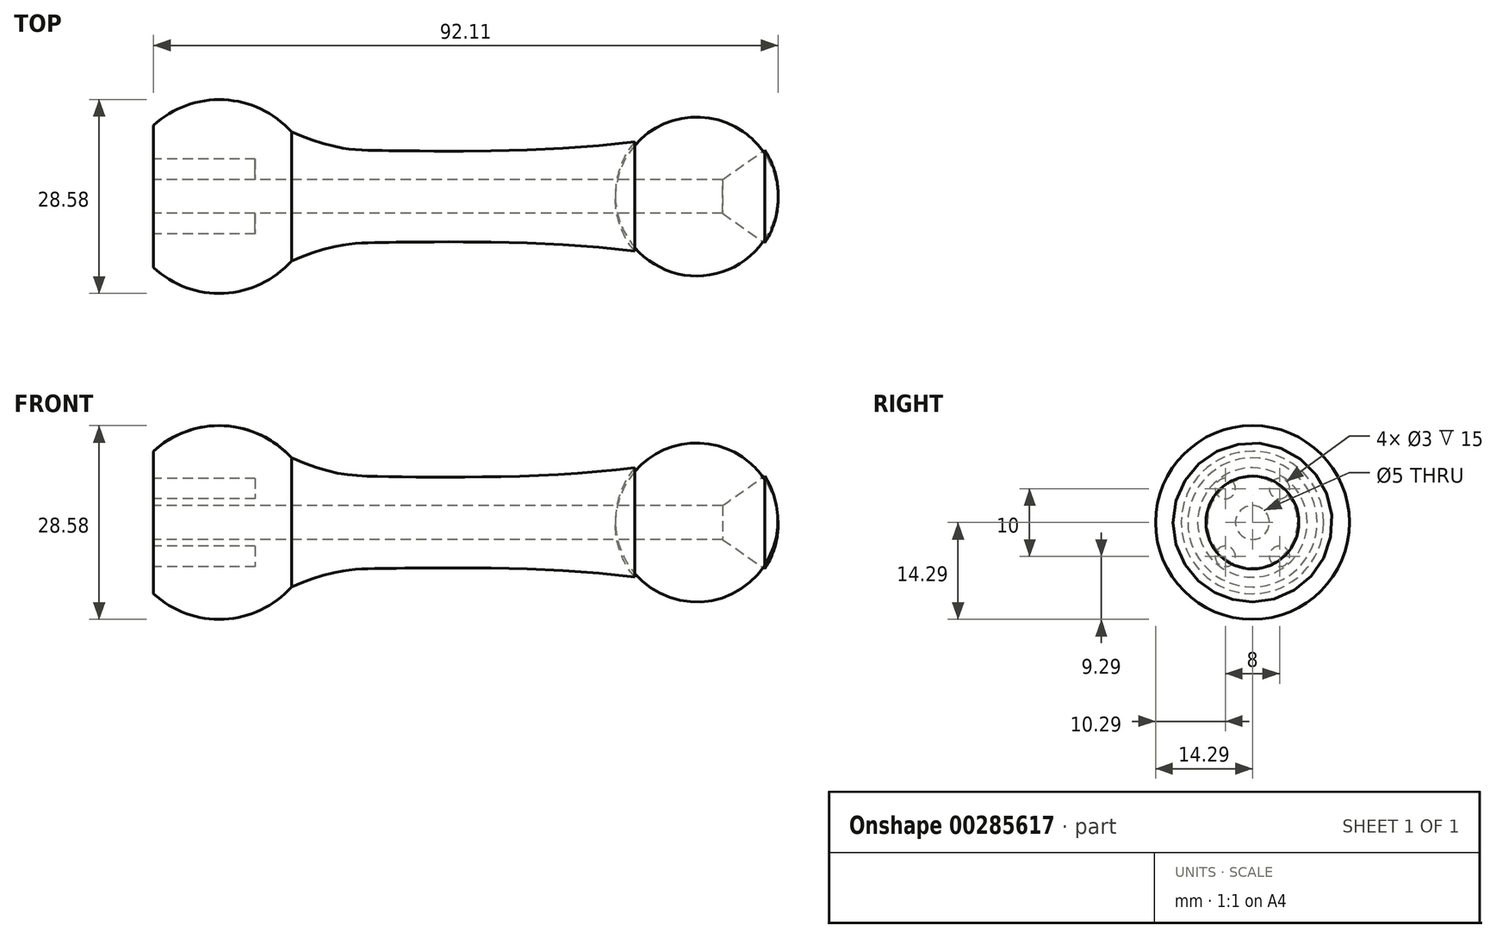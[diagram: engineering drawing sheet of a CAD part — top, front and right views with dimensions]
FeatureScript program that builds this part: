
annotation { "Feature Type Name" : "Feature", "Feature Type Description" : "" }
export const myFeature = defineFeature(function(context is Context, id is Id, definition is map)
    precondition{}
    {
        {
            var Q0;
            Q0=qCreatedBy(makeId("Front.planeOp"),FACE);
            var sketch = newSketch(context, id + "F0", { "sketchPlane" : qUnion([Q0])});
            skLineSegment(sketch, "E0", {"start": v(12.5, 0) * mm, "end": v(57.5, 0) * mm});
            skFitSpline(sketch, "E1", {"points": [v(10.65, 9.52) * mm, v(24.8, 6.77) * mm, v(61.3, 8.08) * mm], "startDerivative": vector(49.03, -20.8) * mm, "endDerivative": vector(62.99, 8.12) * mm});
            skLineSegment(sketch, "E2", {"start": v(12.25, 2.5) * mm, "end": v(74.25, 2.5) * mm});
            skLineSegment(sketch, "E3", {"start": v(74.25, 2.5) * mm, "end": v(80.46, 6.85) * mm});
            skArc(sketch, "E4.trimOffspring", {"start": v(80.46, 6.85) * mm, "mid": v(71.19, 12.25) * mm, "end": v(61.3, 8.08) * mm});
            skPoint(sketch, "E5.end.orphan", {"position": v(82.25, 2.5) * mm});
            skPoint(sketch, "E6.orphan", {"position": v(82.5, 0) * mm});
            skArc(sketch, "E7", {"start": v(10.65, 9.52) * mm, "mid": v(0.69, 14.27) * mm, "end": v(-9.69, 10.5) * mm});
            skLineSegment(sketch, "E8", {"start": v(-9.69, 10.5) * mm, "end": v(-9.69, 2.5) * mm});
            skLineSegment(sketch, "E9", {"start": v(12.25, 2.5) * mm, "end": v(-9.69, 2.5) * mm});
            skSolve(sketch);
        }
        {
            var Q0;
            Q0=makeQuery(id+"F0.imprint","IMPRINT",FACE,{"disambiguationData":[TD([[makeQuery(id+"F0.imprint","IMPRINT",EDGE,{"derivedFrom":sQuery(id+"F0.wireOp",EDGE,"E1")}),-1.0]])]});
            var Q1;
            Q1=sQuery(id+"F0.wireOp",EDGE,"E0");
            revolve(context, id + "F1", {"entities" : qUnion([Q0]), "axis" : qUnion([Q1]), "revolveType" : RevolveType.FULL});
        }
        {
            var Q0;
            Q0=makeQuery(id+"F1.opRevolve","SWEPT_FACE",FACE,{"disambiguationData":[OSD([sQuery(id+"F0.wireOp",EDGE,"E8")])]});
            var sketch = newSketch(context, id + "F2", { "sketchPlane" : qUnion([Q0])});
            skPoint(sketch, "E10.middle", {"position": v(0, 0) * mm});
            skCircle(sketch, "E11", {"center": v(-4, 5) * mm, "radius": 1.5 * mm});
            skCircle(sketch, "E12", {"center": v(4, 5) * mm, "radius": 1.5 * mm});
            skCircle(sketch, "E13", {"center": v(4, -5) * mm, "radius": 1.5 * mm});
            skCircle(sketch, "E14", {"center": v(-4, -5) * mm, "radius": 1.5 * mm});
            skSolve(sketch);
        }
        {
            var Q0;
            Q0=qSketchRegion(id+"F2",true);
            extrude(context, id + "F3", {"entities" : qUnion([Q0]), "operationType" : NewBodyOperationType.REMOVE, "oppositeDirection" : true, "depth" : 15 * mm});
        }
    });
